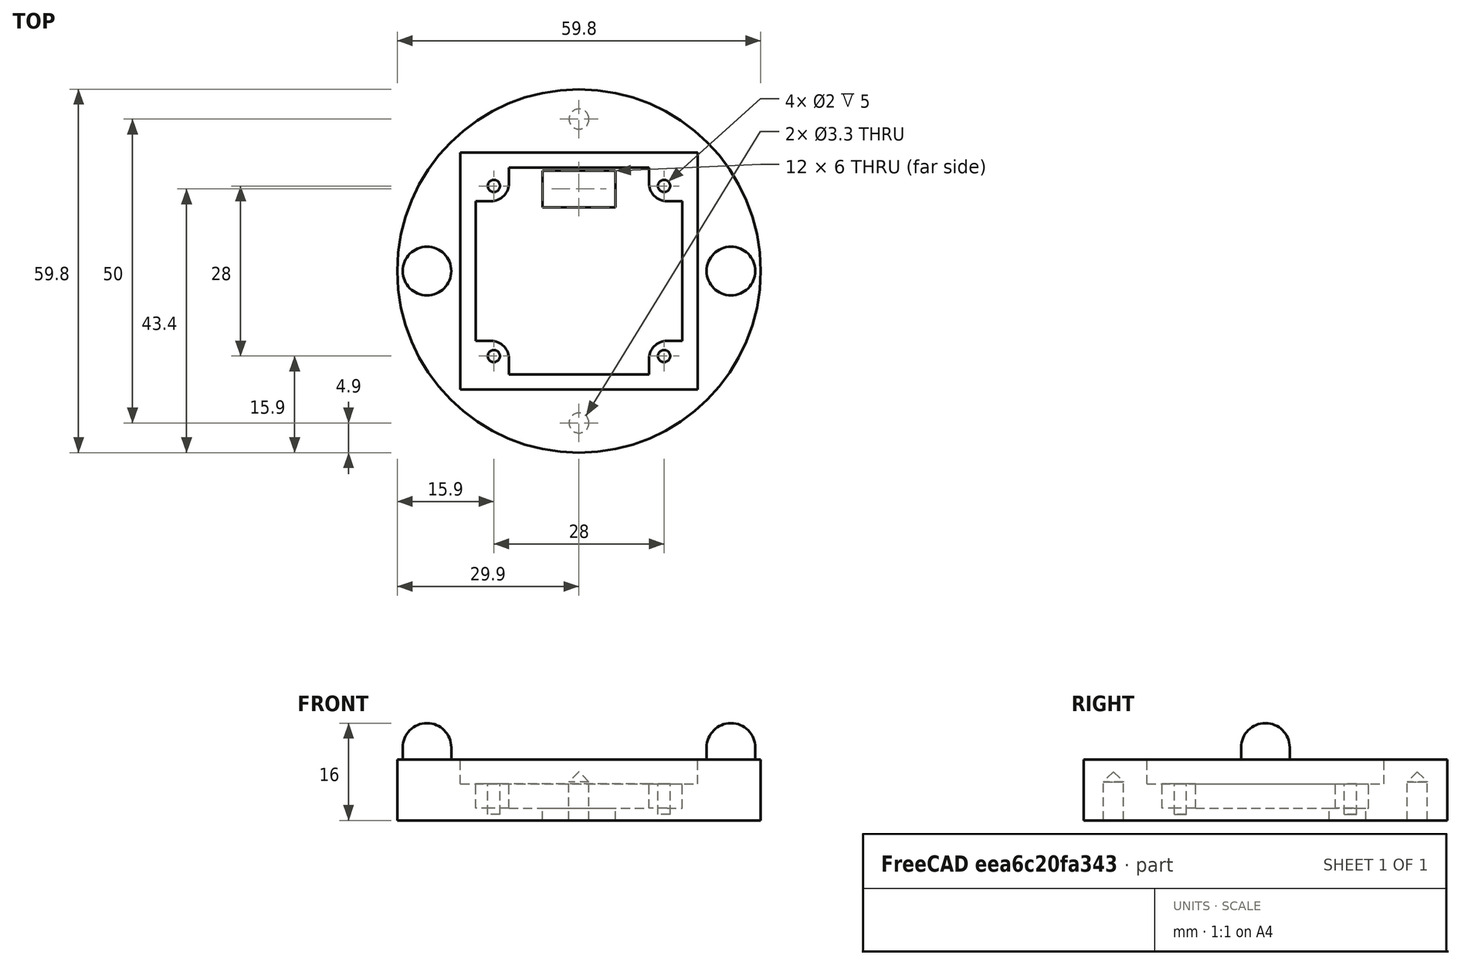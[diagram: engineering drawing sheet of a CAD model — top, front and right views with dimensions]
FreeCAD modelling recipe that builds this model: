
FCSTD DOCUMENT  (FreeCAD 0.18R4 (GitTag))
Label: Kamerhalter_Teil_1
License: All rights reserved
LicenseURL: http://en.wikipedia.org/wiki/All_rights_reserved
objects: Part::Cylinder×9, Part::Fillet×6, Part::Box×4, Part::MultiFuse×3, Part::Cut×3, Part::Chamfer×2
note: 27 computed .brp shape members not serialized (recipe doc carries the construction recipe); baked Part::Feature solids carry a one-line shape summary decoded from their .brp

FEATURE [Part::Box] Box002  label="Rahmen_Aussen"
  AttacherType = Attacher::AttachEngine3D
  Height = 4
  Length = 39
  Placement = pos=(-19.5,-19.5,6) rot=(0,0,1;0rad)
  Width = 39
FEATURE [Part::Box] Box003  label="Rahmen_Innen"
  AttacherType = Attacher::AttachEngine3D
  Height = 8
  Length = 34
  Placement = pos=(-17,-17,2) rot=(0,0,1;0rad)
  Width = 34
FEATURE [Part::Box] Box004  label="Würfel_Eck"
  AttacherType = Attacher::AttachEngine3D
  Height = 4
  Length = 5.5
  Placement = pos=(11.5,11.5,2) rot=(0,0,1;0rad)
  Width = 5.5
FEATURE [Part::Fillet] Fillet  label="Ecke_001"
  Base = -> Box004
  Edges = 1 edges r=3: [Edge1]
FEATURE [Part::Fillet] Fillet001  label="Ecke_002"
  Base = -> Box004
  Edges = 1 edges r=3: [Edge1]
  Placement = pos=(0,0,0) rot=(0,0,1;1.5708rad)
FEATURE [Part::Fillet] Fillet002  label="Ecke_003"
  Base = -> Box004
  Edges = 1 edges r=3: [Edge1]
  Placement = pos=(0,0,0) rot=(0,0,1;3.14159rad)
FEATURE [Part::Fillet] Fillet003  label="Ecke_004"
  Base = -> Box004
  Edges = 1 edges r=3: [Edge1]
  Placement = pos=(0,0,0) rot=(0,0,-1;1.5708rad)
FEATURE [Part::Cylinder] Cylinder  label="Bohrloch_001"
  Angle = 360
  AttacherType = Attacher::AttachEngine3D
  Height = 5
  Placement = pos=(14,14,1) rot=(0,0,1;0rad)
  Radius = 1
FEATURE [Part::Cylinder] Cylinder001  label="Bohrloch_002"
  Angle = 360
  AttacherType = Attacher::AttachEngine3D
  Height = 5
  Placement = pos=(-14,14,1) rot=(0,0,1;0rad)
  Radius = 1
FEATURE [Part::Cylinder] Cylinder002  label="Bohrloch_003"
  Angle = 360
  AttacherType = Attacher::AttachEngine3D
  Height = 5
  Placement = pos=(-14,-14,1) rot=(0,0,1;0rad)
  Radius = 1
FEATURE [Part::Cylinder] Cylinder003  label="Bohrloch_004"
  Angle = 360
  AttacherType = Attacher::AttachEngine3D
  Height = 5
  Placement = pos=(14,-14,1) rot=(0,0,1;0rad)
  Radius = 1
FEATURE [Part::MultiFuse] Fusion001  label="Ecken"
  Shapes = -> [Fillet003,Fillet002,Fillet001,Fillet]
FEATURE [Part::Cylinder] Cylinder004  label="Kreis_Aussen"
  Angle = 360
  AttacherType = Attacher::AttachEngine3D
  Height = 10
  Radius = 29.9
FEATURE [Part::Cut] Cut  label="Schnitt_003"
  Base = -> Cylinder004
  Tool = -> Box002
FEATURE [Part::Cut] Cut001  label="Schnitt_002"
  Base = -> Cut
  Tool = -> Box003
FEATURE [Part::Box] Box  label="Aussparung_USB_Kabel"
  AttacherType = Attacher::AttachEngine3D
  Height = 2
  Length = 12
  Placement = pos=(-6,10.5,0) rot=(0,0,1;0rad)
  Width = 6
FEATURE [Part::Cylinder] Cylinder006  label="Justiernoppen_002"
  Angle = 360
  AttacherType = Attacher::AttachEngine3D
  Height = 6
  Placement = pos=(-25,0,10) rot=(0,0,1;0rad)
  Radius = 4
FEATURE [Part::Cylinder] Cylinder008  label="Justiernoppen_001"
  Angle = 360
  AttacherType = Attacher::AttachEngine3D
  Height = 6
  Placement = pos=(25,0,10) rot=(0,0,1;0rad)
  Radius = 4
FEATURE [Part::Cylinder] Cylinder009  label="Bohrloch_007"
  Angle = 360
  AttacherType = Attacher::AttachEngine3D
  Height = 8
  Placement = pos=(0,-25,0) rot=(0,0,1;0rad)
  Radius = 1.65
FEATURE [Part::Cylinder] Cylinder010  label="Bohrloch_008"
  Angle = 360
  AttacherType = Attacher::AttachEngine3D
  Height = 8
  Placement = pos=(0,25,0) rot=(0,0,1;0rad)
  Radius = 1.65
FEATURE [Part::Chamfer] Chamfer  label="Chamfer001"
  Base = -> Cylinder009
  Edges = 1 edges r=1.65: [Edge1]
FEATURE [Part::Chamfer] Chamfer001  label="Chamfer002"
  Base = -> Cylinder010
  Edges = 1 edges r=1.65: [Edge1]
FEATURE [Part::MultiFuse] Fusion  label="Bohrloecher"
  Shapes = -> [Cylinder,Cylinder003,Cylinder001,Cylinder002,Box,Chamfer,Chamfer001]
FEATURE [Part::Fillet] Fillet004
  Base = -> Cylinder006
  Edges = 1 edges r=4: [Edge1]
FEATURE [Part::Fillet] Fillet005
  Base = -> Cylinder008
  Edges = 1 edges r=4: [Edge1]
FEATURE [Part::MultiFuse] Fusion002  label="Grundform_001"
  Shapes = -> [Fusion001,Cut001,Fillet004,Fillet005]
FEATURE [Part::Cut] Cut002  label="Schnitt_001"
  Base = -> Fusion002
  Tool = -> Fusion
